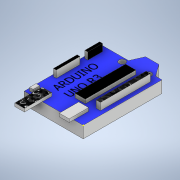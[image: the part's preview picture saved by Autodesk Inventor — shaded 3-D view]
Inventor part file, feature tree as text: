
AUTODESK INVENTOR PART (.ipt)
format: ipt  version: 2021 (Build 250183000, 183)  size: 171,520 bytes
history: native  units: mm
features: sketch x7, extrude x5, hole x1
ambient origin geometry x8: Origin, YZ Plane, XZ Plane, XY Plane, X Axis, Y Axis, Z Axis, Center Point
bodies: Solid1 (feature_tree)
feature tree (13):
  extrude  "Extrusion1"  Depth=75.0mm
  extrude  "Extrusion2"  Depth=9.0mm TaperAngle=0.0deg
  extrude  "Extrusion3"  Depth=4.0mm TaperAngle=0.0deg
  extrude  "Extrusion4"  Depth=10.0mm
  extrude  "Extrusion5"  Depth=0.0625mm
  sketch  "Sketch6"  dims[d20=20.594885mm d21=0.0625mm]
  hole  "Hole1"  [1 undecoded]
  sketch  "Sketch1"  dims[d0=100.0mm d1=75.0mm]
  sketch  "Sketch2"  dims[d2=15.0mm d3=0.0mm d4=9.0mm d5=0.0mm]
  sketch  "Sketch3"  dims[d6=9.0mm d7=0.0mm d8=4.0mm d9=0.0mm]
  sketch  "Sketch4"  dims[d10=5.0mm d11=0.0mm]
  sketch  "Sketch5"  dims[d12=8.0mm d13=6.0mm d14=4.0mm d15=2.0mm d16=90.0deg d17=10.0mm d18=0.0mm d19=0.75mm]
  sketch  "Sketch7"  dims[d22=0.75mm d23=0.375mm]
note: 1 required parameter value undecoded (feature->parameter linkage not recoverable at this tier; creation-order binding heuristic only, values carry confidence <= 0.55)
